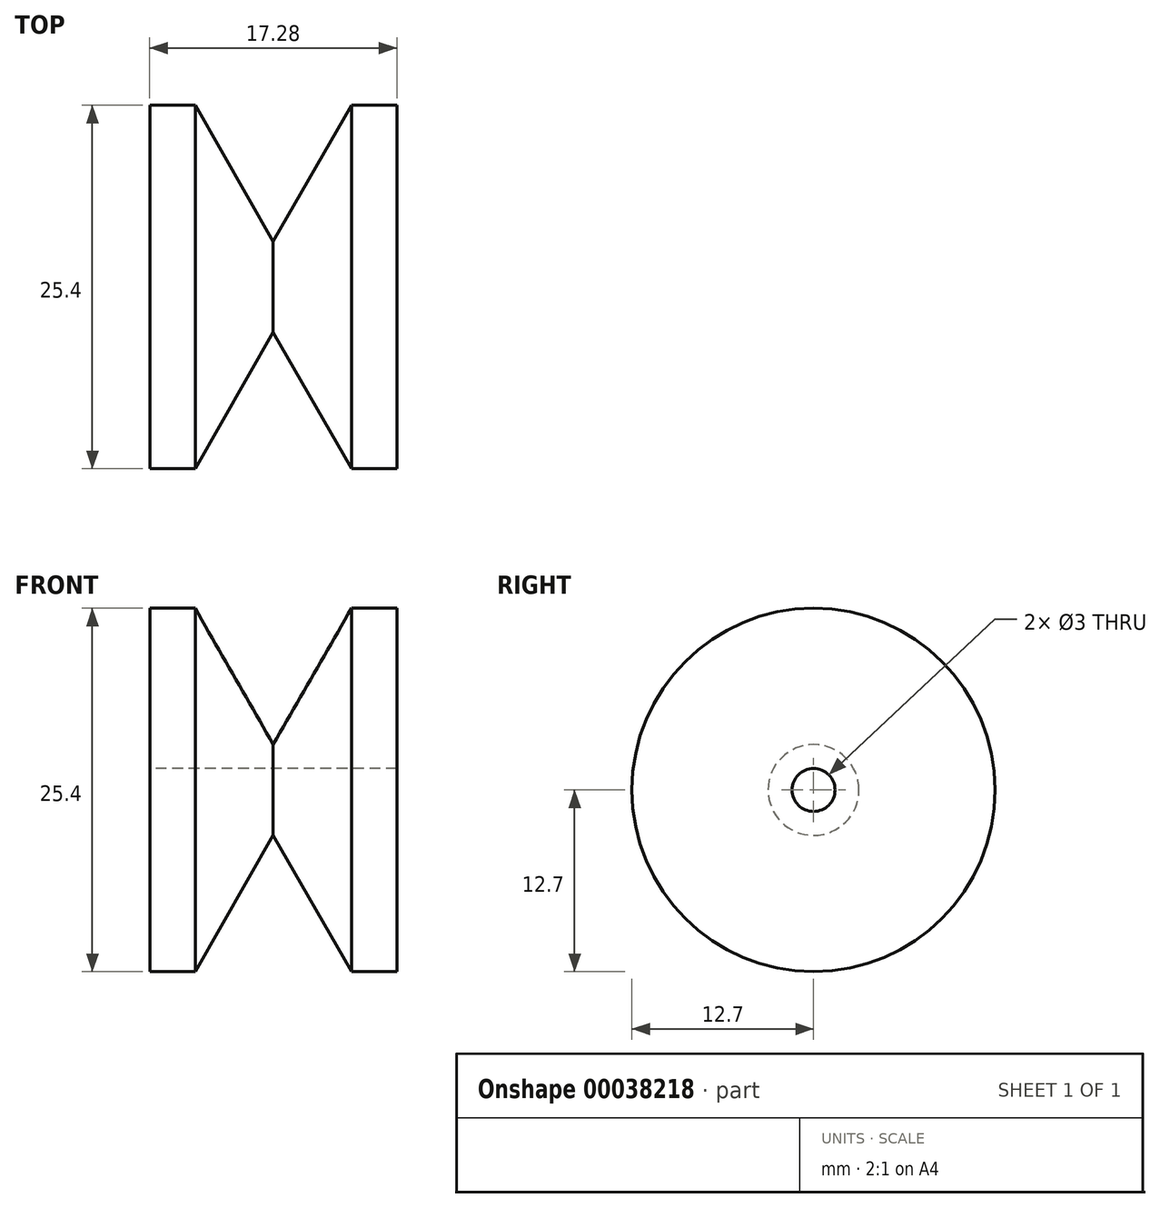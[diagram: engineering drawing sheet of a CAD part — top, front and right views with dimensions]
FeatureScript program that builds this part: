
annotation { "Feature Type Name" : "Feature", "Feature Type Description" : "" }
export const myFeature = defineFeature(function(context is Context, id is Id, definition is map)
    precondition{}
    {
        {
            var Q0;
            Q0=qCreatedBy(makeId("Front.planeOp"),FACE);
            var sketch = newSketch(context, id + "F0", { "sketchPlane" : qUnion([Q0])});
            skLineSegment(sketch, "E0", {"start": v(-8.64, 12.7) * mm, "end": v(-5.46, 12.7) * mm});
            skLineSegment(sketch, "E1", {"start": v(-5.46, 12.7) * mm, "end": v(0, 3.17) * mm});
            skLineSegment(sketch, "E2", {"start": v(0, 3.17) * mm, "end": v(5.46, 12.7) * mm});
            skLineSegment(sketch, "E3", {"start": v(-8.64, 12.7) * mm, "end": v(-8.64, 1.5) * mm});
            skLineSegment(sketch, "E4", {"start": v(8.64, 12.7) * mm, "end": v(8.64, 1.5) * mm});
            skLineSegment(sketch, "E5", {"start": v(-8.64, 1.5) * mm, "end": v(16.76, 1.5) * mm});
            skLineSegment(sketch, "E6", {"start": v(8.64, 12.7) * mm, "end": v(5.46, 12.7) * mm});
            skLineSegment(sketch, "E7", {"start": v(-8.64, 0) * mm, "end": v(8.64, 0) * mm, "construction": true});
            skSolve(sketch);
        }
        {
            var Q0;
            Q0=makeQuery(id+"F0.imprint","IMPRINT",FACE,{"disambiguationData":[TD([[makeQuery(id+"F0.imprint","IMPRINT",EDGE,{"derivedFrom":sQuery(id+"F0.wireOp",EDGE,"E0")}),-1.0]])]});
            var Q1;
            Q1=sQuery(id+"F0.wireOp",EDGE,"E7");
            revolve(context, id + "F1", {"entities" : qUnion([Q0]), "axis" : qUnion([Q1]), "revolveType" : RevolveType.FULL});
        }
    });
